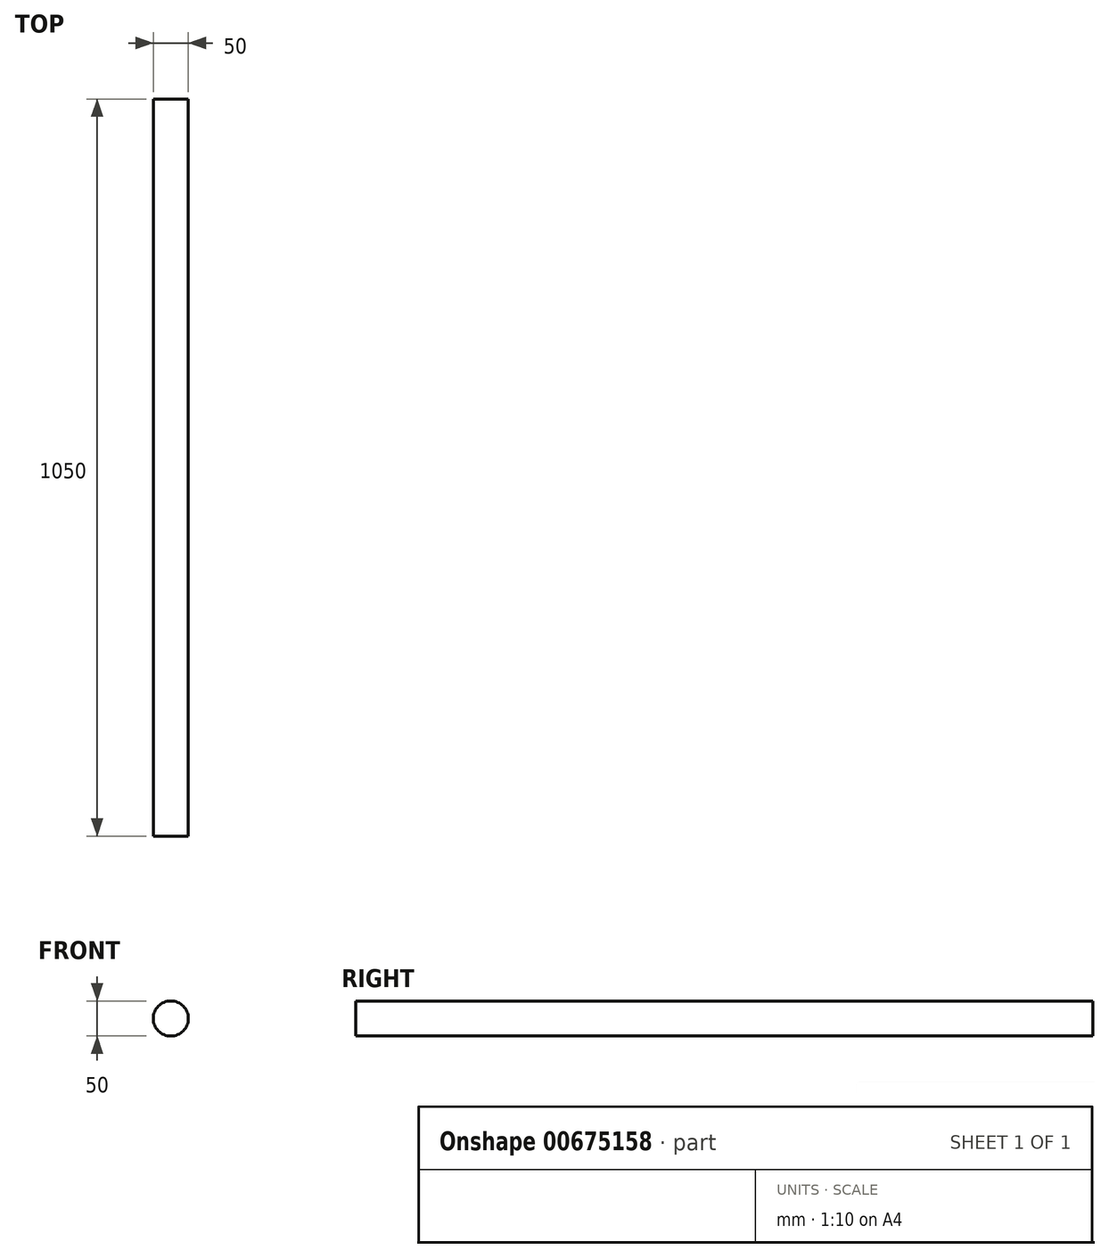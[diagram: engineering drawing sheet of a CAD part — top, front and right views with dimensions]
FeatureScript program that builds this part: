
annotation { "Feature Type Name" : "Feature", "Feature Type Description" : "" }
export const myFeature = defineFeature(function(context is Context, id is Id, definition is map)
    precondition{}
    {
        {
            var Q0;
            Q0=qCreatedBy(makeId("Front.planeOp"),FACE);
            var sketch = newSketch(context, id + "F0", { "sketchPlane" : qUnion([Q0])});
            skCircle(sketch, "E0", {"center": v(0, 0) * mm, "radius": 25 * mm});
            skSolve(sketch);
        }
        {
            var Q0;
            Q0=makeQuery(id+"F0.imprint","IMPRINT",FACE,{"disambiguationData":[TD([[makeQuery(id+"F0.imprint","IMPRINT",EDGE,{"derivedFrom":sQuery(id+"F0.wireOp",EDGE,"E0")}),1.0]])]});
            extrude(context, id + "F1", {"entities" : qUnion([Q0]), "depth" : 950 * mm, "offsetDistance" : 25 * mm});
        }
        {
            var Q0;
            Q0 = qSketchRegion(id + "F0", true);
            extrude(context, id + "F2", {"entities" : qUnion([Q0]), "operationType" : NewBodyOperationType.ADD, "oppositeDirection" : true, "depth" : 100 * mm, "offsetDistance" : 25 * mm});
        }
    });
